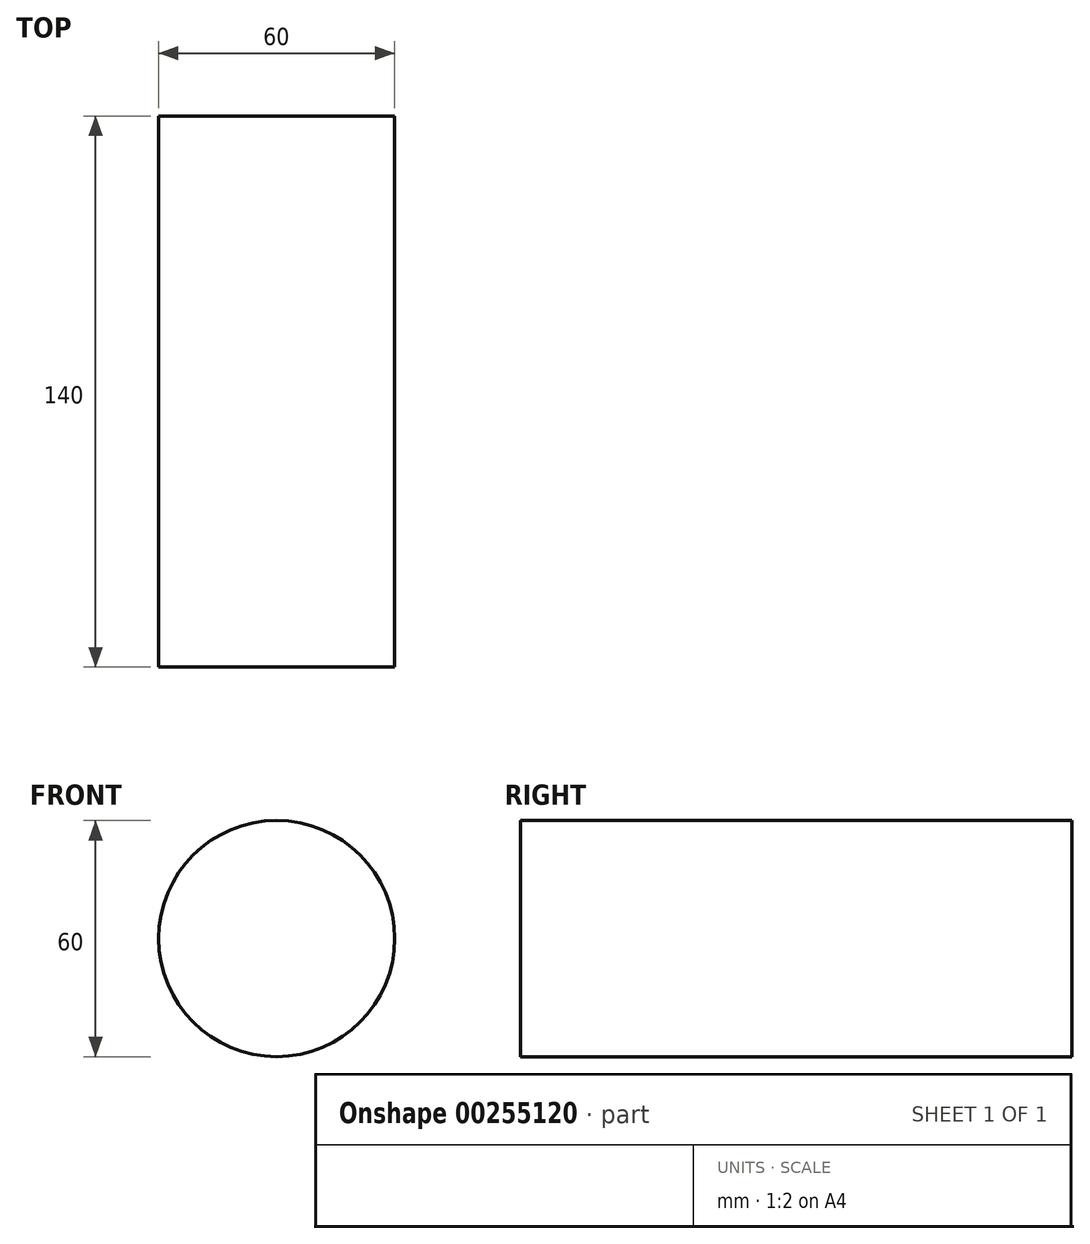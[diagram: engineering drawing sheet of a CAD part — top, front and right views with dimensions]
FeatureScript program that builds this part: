
annotation { "Feature Type Name" : "Feature", "Feature Type Description" : "" }
export const myFeature = defineFeature(function(context is Context, id is Id, definition is map)
    precondition{}
    {
        {
            var Q0;
            Q0=qCreatedBy(makeId("Front.planeOp"),FACE);
            var sketch = newSketch(context, id + "F0", { "sketchPlane" : qUnion([Q0])});
            skCircle(sketch, "E0", {"center": v(0, 0) * mm, "radius": 30 * mm});
            skSolve(sketch);
        }
        {
            var Q0;
            Q0 = qSketchRegion(id + "F0", true);
            extrude(context, id + "F1", {"entities" : qUnion([Q0]), "oppositeDirection" : true, "depth" : 140 * mm, "offsetDistance" : 25 * mm});
        }
    });
